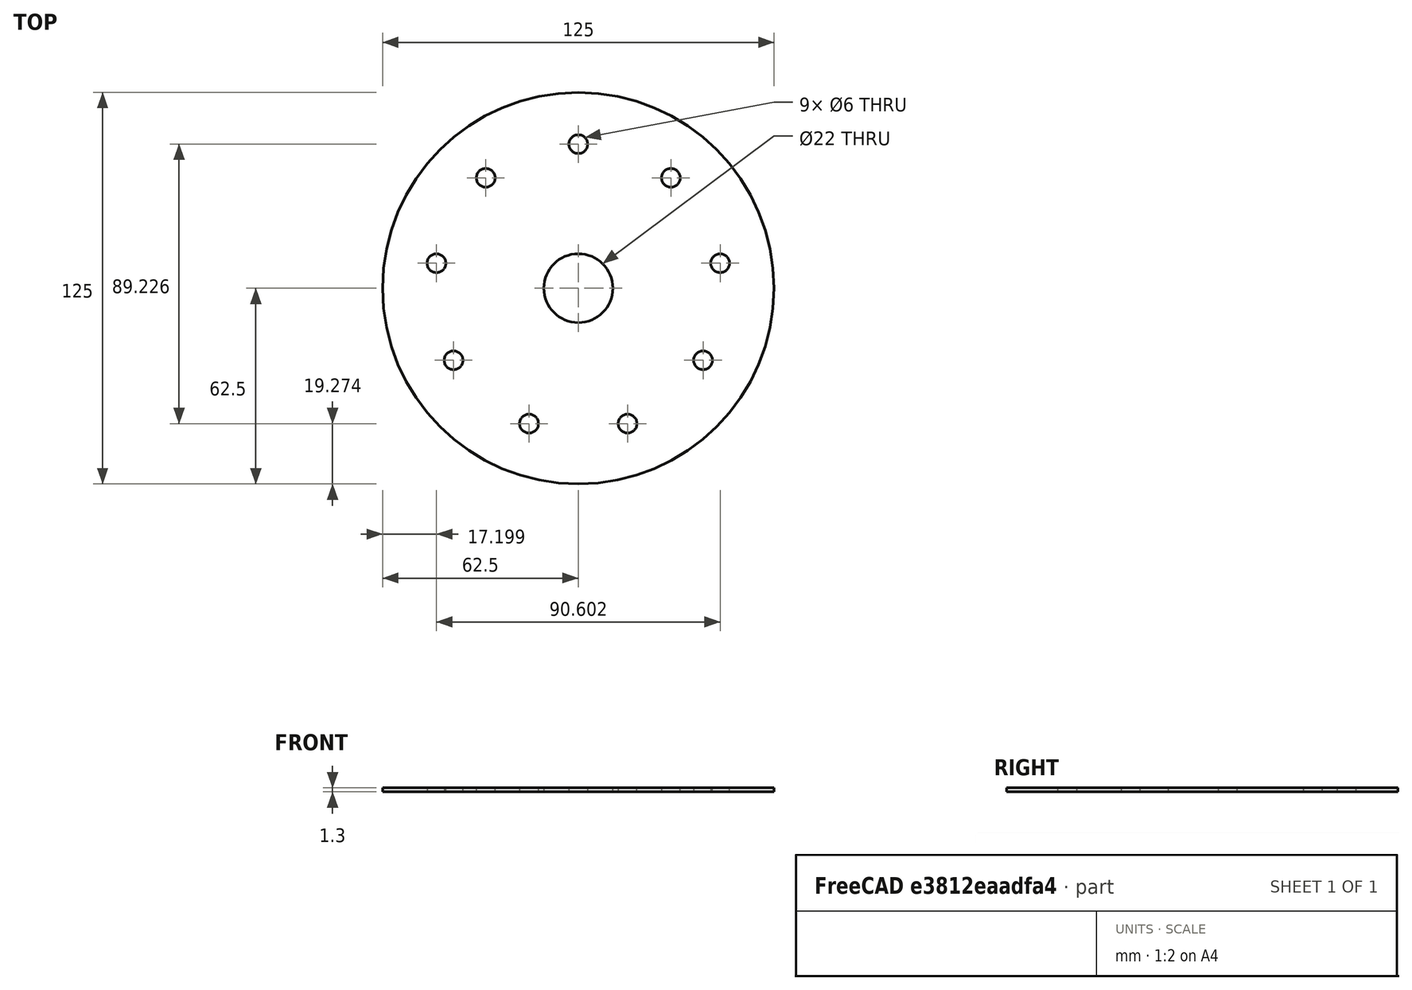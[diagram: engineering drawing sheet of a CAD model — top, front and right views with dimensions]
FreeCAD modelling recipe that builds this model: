
FCSTD DOCUMENT  (FreeCAD 0.19R24276 (Git))
Label: Disk_bolgarki_d22_d125
License: All rights reserved
LicenseURL: http://en.wikipedia.org/wiki/All_rights_reserved
objects: Sketcher::SketchObject×1, PartDesign::Pad×1, PartDesign::Body×1
note: 4 computed .brp shape members not serialized (recipe doc carries the construction recipe); baked Part::Feature solids carry a one-line shape summary decoded from their .brp

FEATURE [Sketcher::SketchObject] Sketch
  FullyConstrained = true
  MapMode = 5
  Support = -> [XY_Plane]
  sketch-geometry (21):
    g0: Circle CenterX=0 CenterY=0 CenterZ=0 NormalX=0 NormalY=0 NormalZ=1 AngleXU=0 Radius=11
    g1: Circle CenterX=0 CenterY=0 CenterZ=0 NormalX=0 NormalY=0 NormalZ=1 AngleXU=0 Radius=62.5
    g2: LineSegment StartX=0 StartY=46 StartZ=0 EndX=-29.5682 EndY=35.238 EndZ=0
    g3: LineSegment StartX=-29.5682 StartY=35.238 StartZ=0 EndX=-45.3012 EndY=7.98782 EndZ=0
    g4: LineSegment StartX=-45.3012 StartY=7.98782 StartZ=0 EndX=-39.8372 EndY=-23 EndZ=0
    g5: LineSegment StartX=-39.8372 StartY=-23 StartZ=0 EndX=-15.7329 EndY=-43.2259 EndZ=0
    g6: LineSegment StartX=-15.7329 StartY=-43.2259 StartZ=0 EndX=15.7329 EndY=-43.2259 EndZ=0
    g7: LineSegment StartX=15.7329 StartY=-43.2259 StartZ=0 EndX=39.8372 EndY=-23 EndZ=0
    g8: LineSegment StartX=39.8372 StartY=-23 StartZ=0 EndX=45.3012 EndY=7.98782 EndZ=0
    g9: LineSegment StartX=45.3012 StartY=7.98782 StartZ=0 EndX=29.5682 EndY=35.238 EndZ=0
    g10: LineSegment StartX=29.5682 StartY=35.238 StartZ=0 EndX=0 EndY=46 EndZ=0
    g11: Circle CenterX=0 CenterY=0 CenterZ=0 NormalX=0 NormalY=0 NormalZ=1 AngleXU=0 Radius=46
    g12: Circle CenterX=0 CenterY=46 CenterZ=0 NormalX=0 NormalY=0 NormalZ=1 AngleXU=0 Radius=3
    g13: Circle CenterX=29.5682 CenterY=35.238 CenterZ=0 NormalX=0 NormalY=0 NormalZ=1 AngleXU=0 Radius=3
    g14: Circle CenterX=45.3012 CenterY=7.98782 CenterZ=0 NormalX=0 NormalY=0 NormalZ=1 AngleXU=0 Radius=3
    g15: Circle CenterX=39.8372 CenterY=-23 CenterZ=0 NormalX=0 NormalY=0 NormalZ=1 AngleXU=0 Radius=3
    g16: Circle CenterX=15.7329 CenterY=-43.2259 CenterZ=0 NormalX=0 NormalY=0 NormalZ=1 AngleXU=0 Radius=3
    g17: Circle CenterX=-15.7329 CenterY=-43.2259 CenterZ=0 NormalX=0 NormalY=0 NormalZ=1 AngleXU=0 Radius=3
    g18: Circle CenterX=-39.8372 CenterY=-23 CenterZ=0 NormalX=0 NormalY=0 NormalZ=1 AngleXU=0 Radius=3
    g19: Circle CenterX=-45.3012 CenterY=7.98782 CenterZ=0 NormalX=0 NormalY=0 NormalZ=1 AngleXU=0 Radius=3
    g20: Circle CenterX=-29.5682 CenterY=35.238 CenterZ=0 NormalX=0 NormalY=0 NormalZ=1 AngleXU=0 Radius=3
  constraints (44):
    c: Coincident(g0,g-1)
    c: Coincident(g1,g0)
    c: Coincident(g2,g3)
    c: Coincident(g3,g4)
    c: Coincident(g4,g5)
    c: Coincident(g5,g6)
    c: Coincident(g6,g7)
    c: Coincident(g7,g8)
    c: Coincident(g8,g9)
    c: Coincident(g9,g10)
    c: Coincident(g10,g2)
    c: Equal(g2, g3-g10) x8
    c: PointOnObject(g2,g11)
    c: PointOnObject(g3,g11)
    c: PointOnObject(g4,g11)
    c: PointOnObject(g5,g11)
    c: PointOnObject(g6,g11)
    c: PointOnObject(g7,g11)
    c: PointOnObject(g8,g11)
    c: PointOnObject(g9,g11)
    c: PointOnObject(g10,g11)
    c: Coincident(g11,g0)
    c: PointOnObject(g10,g-2)
    c: Diameter(g11) = 92
    c: Diameter(g0) = 22
    c: Diameter(g1) = 125
    c: Coincident(g12,g2)
    c: Diameter(g12) = 6
    c: Coincident(g13,g9)
    c: Coincident(g14,g8)
    c: Coincident(g15,g7)
    c: Coincident(g16,g6)
    c: Coincident(g17,g5)
    c: Coincident(g18,g4)
    c: Coincident(g19,g3)
    c: Coincident(g20,g2)
    c: Equal(g20,g13)
    c: Equal(g13,g14)
    c: Equal(g14,g15)
    c: Equal(g15,g16)
    c: Equal(g16,g17)
    c: Equal(g17,g18)
    c: Equal(g18,g19)
    c: Equal(g19,g12)
FEATURE [PartDesign::Pad] Pad
  Direction = (1,1,1)
  Length = 1.3
  Length2 = 100
  Profile = -> Sketch
  Type = 0
FEATURE [PartDesign::Body] Body
  Group = -> [Sketch,Pad]
  Origin = -> Origin
  Tip = -> Pad
